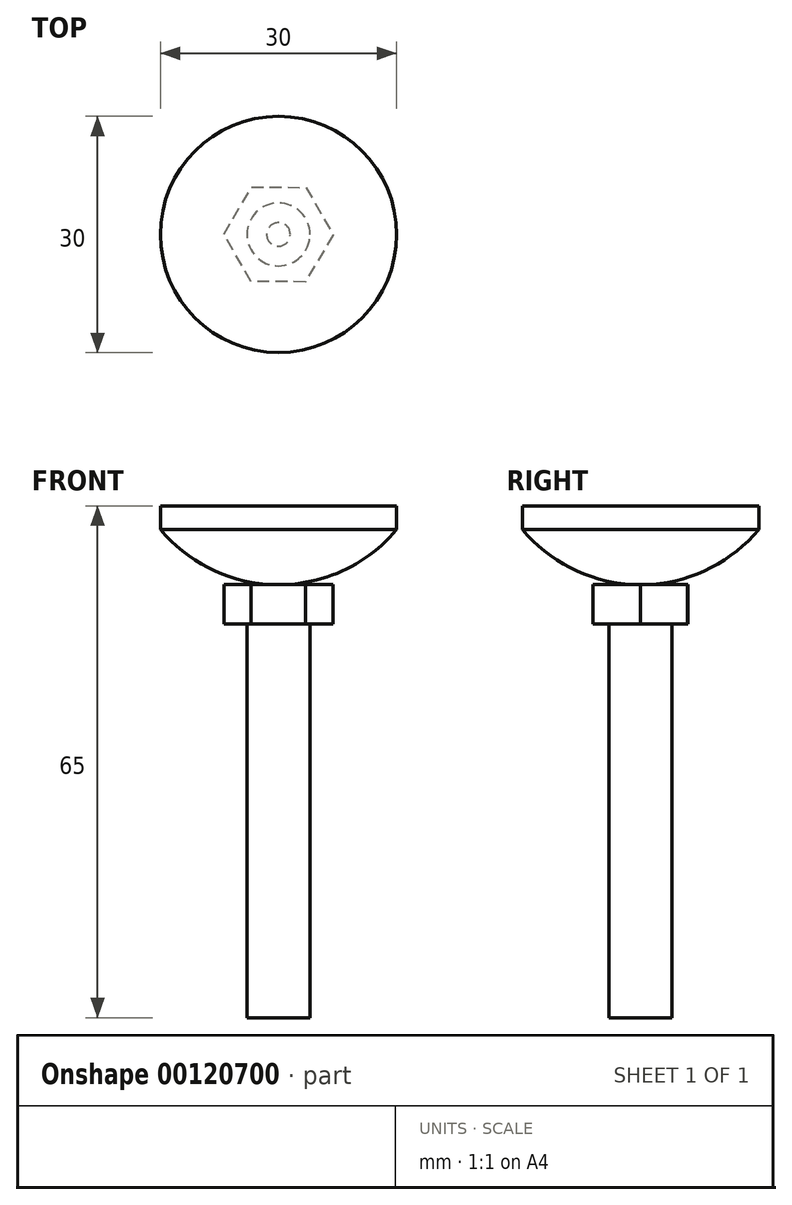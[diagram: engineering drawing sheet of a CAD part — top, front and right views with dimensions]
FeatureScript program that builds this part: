
annotation { "Feature Type Name" : "Feature", "Feature Type Description" : "" }
export const myFeature = defineFeature(function(context is Context, id is Id, definition is map)
    precondition{}
    {
        {
            var Q0;
            Q0=qCreatedBy(makeId("Top.planeOp"),FACE);
            var sketch = newSketch(context, id + "F0", { "sketchPlane" : qUnion([Q0])});
            skCircle(sketch, "E0", {"center": v(0, 0) * mm, "radius": 4 * mm});
            skSolve(sketch);
        }
        {
            var Q0;
            Q0 = qSketchRegion(id + "F0", true);
            extrude(context, id + "F1", {"entities" : qUnion([Q0]), "depth" : 50 * mm});
        }
        {
            var Q0;
            Q0=makeQuery(id+"F1.opExtrude","CAP_FACE",FACE,{"disambiguationData":[OSD([sQuery(id+"F0.wireOp",EDGE,"E0")])],"isStart":false});
            var sketch = newSketch(context, id + "F2", { "sketchPlane" : qUnion([Q0])});
            skCircle(sketch, "E1.cCircle", {"center": v(0, 0) * mm, "radius": 6 * mm, "construction": true});
            skLineSegment(sketch, "E1.0", {"start": v(3.5, 5.97) * mm, "end": v(6.93, -0.05) * mm});
            skLineSegment(sketch, "E1.1", {"start": v(6.93, -0.05) * mm, "end": v(3.42, -6.03) * mm});
            skLineSegment(sketch, "E1.2", {"start": v(3.42, -6.03) * mm, "end": v(-3.5, -5.97) * mm});
            skLineSegment(sketch, "E1.3", {"start": v(-3.5, -5.97) * mm, "end": v(-6.93, 0.05) * mm});
            skLineSegment(sketch, "E1.4", {"start": v(-6.93, 0.05) * mm, "end": v(-3.42, 6.03) * mm});
            skLineSegment(sketch, "E1.5", {"start": v(-3.42, 6.03) * mm, "end": v(3.5, 5.97) * mm});
            skPoint(sketch, "E1.0.midPoint", {"position": v(5.22, 2.96) * mm});
            skSolve(sketch);
        }
        {
            var Q0;
            Q0 = qSketchRegion(id + "F2", true);
            extrude(context, id + "F3", {"entities" : qUnion([Q0]), "operationType" : NewBodyOperationType.ADD, "depth" : 5 * mm});
        }
        {
            var Q0;
            Q0=makeQuery(id+"F3.opExtrude","CAP_FACE",FACE,{"disambiguationData":[OSD([sQuery(id+"F2.wireOp",EDGE,"E1.0"),sQuery(id+"F2.wireOp",EDGE,"E1.1"),sQuery(id+"F2.wireOp",EDGE,"E1.2"),sQuery(id+"F2.wireOp",EDGE,"E1.3"),sQuery(id+"F2.wireOp",EDGE,"E1.4"),sQuery(id+"F2.wireOp",EDGE,"E1.5")])],"isStart":false});
            var sketch = newSketch(context, id + "F4", { "sketchPlane" : qUnion([Q0])});
            skCircle(sketch, "E2", {"center": v(0, 0) * mm, "radius": 1.5 * mm});
            skSolve(sketch);
        }
        {
            var Q0;
            Q0 = qSketchRegion(id + "F4", true);
            extrude(context, id + "F5", {"entities" : qUnion([Q0]), "operationType" : NewBodyOperationType.ADD, "depth" : 5 * mm});
        }
        {
            var Q0;
            Q0=qCreatedBy(makeId("Front.planeOp"),FACE);
            var sketch = newSketch(context, id + "F6", { "sketchPlane" : qUnion([Q0])});
            skArc(sketch, "E3", {"start": v(-15, 62) * mm, "mid": v(-8.28, 56.84) * mm, "end": v(0, 55) * mm});
            skLineSegment(sketch, "E4", {"start": v(0, 0) * mm, "end": v(0, 65.46) * mm, "construction": true});
            skLineSegment(sketch, "E5", {"start": v(-15, 62) * mm, "end": v(-15, 65) * mm});
            skLineSegment(sketch, "E6", {"start": v(-15, 65) * mm, "end": v(0, 65) * mm});
            skLineSegment(sketch, "E7", {"start": v(0, 65) * mm, "end": v(0, 55) * mm});
            skSolve(sketch);
        }
        {
            var Q0;
            Q0 = qSketchRegion(id + "F6", true);
            var Q1;
            Q1=sQuery(id+"F6.wireOp",EDGE,"E7");
            revolve(context, id + "F7", {"operationType" : NewBodyOperationType.ADD, "entities" : qUnion([Q0]), "axis" : qUnion([Q1]), "revolveType" : RevolveType.FULL});
        }
    });
